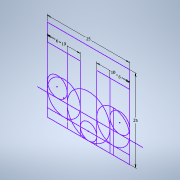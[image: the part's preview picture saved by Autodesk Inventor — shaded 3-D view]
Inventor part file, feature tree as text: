
AUTODESK INVENTOR PART (.ipt)
format: ipt  version: 2022.3 (Build 263350000, 350)  size: 100,864 bytes
history: native  units: mm
features: sketch x1
ambient origin geometry x8: Origin, YZ Plane, XZ Plane, XY Plane, X Axis, Y Axis, Z Axis, Center Point
feature tree (1):
  sketch  "Sketch1"  dims[d0=25.0mm d1=25.0mm d2=10.0mm d3=10.0mm d4=6.0mm d5=6.0mm]
